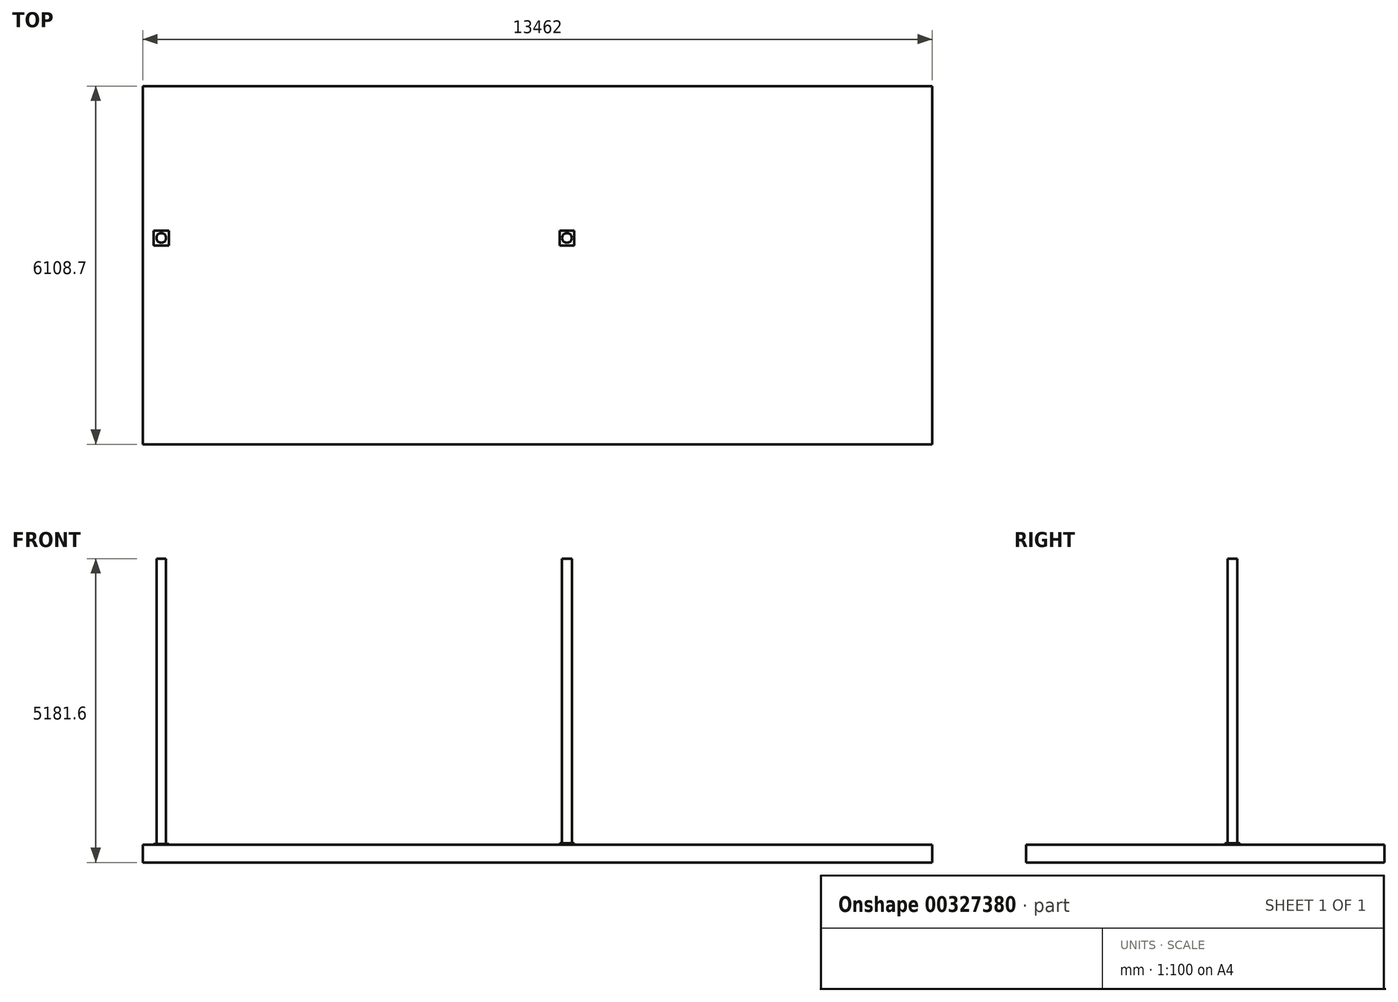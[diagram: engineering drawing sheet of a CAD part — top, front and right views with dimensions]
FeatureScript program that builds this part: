
annotation { "Feature Type Name" : "Feature", "Feature Type Description" : "" }
export const myFeature = defineFeature(function(context is Context, id is Id, definition is map)
    precondition{}
    {
        {
            var Q0;
            Q0=qCreatedBy(makeId("Top.planeOp"),FACE);
            var sketch = newSketch(context, id + "F0", { "sketchPlane" : qUnion([Q0])});
            skLineSegment(sketch, "E0.bottom", {"start": v(0, 0) * mm, "end": v(13462, 0) * mm});
            skLineSegment(sketch, "E0.top", {"start": v(0, 6108.7) * mm, "end": v(13462, 6108.7) * mm});
            skLineSegment(sketch, "E0.left", {"start": v(0, 0) * mm, "end": v(0, 6108.7) * mm});
            skLineSegment(sketch, "E0.right", {"start": v(13462, 0) * mm, "end": v(13462, 6108.7) * mm});
            skSolve(sketch);
        }
        {
            var Q0;
            Q0=makeQuery(id+"F0.imprint","IMPRINT",FACE,{"disambiguationData":[TD([[makeQuery(id+"F0.imprint","IMPRINT",EDGE,{"derivedFrom":sQuery(id+"F0.wireOp",EDGE,"E0.bottom")}),1.0]])]});
            extrude(context, id + "F1", {"entities" : qUnion([Q0]), "oppositeDirection" : true, "depth" : 304.8 * mm});
        }
        {
            var Q0;
            Q0=makeQuery(id+"F1.opExtrude","CAP_FACE",FACE,{"disambiguationData":[OSD([sQuery(id+"F0.wireOp",EDGE,"E0.bottom"),sQuery(id+"F0.wireOp",EDGE,"E0.top"),sQuery(id+"F0.wireOp",EDGE,"E0.left"),sQuery(id+"F0.wireOp",EDGE,"E0.right")])],"isStart":true});
            var sketch = newSketch(context, id + "F2", { "sketchPlane" : qUnion([Q0])});
            skLineSegment(sketch, "E1.bottom", {"start": v(190.5, 3644.9) * mm, "end": v(444.5, 3644.9) * mm});
            skLineSegment(sketch, "E1.top", {"start": v(190.5, 3390.9) * mm, "end": v(444.5, 3390.9) * mm});
            skLineSegment(sketch, "E1.left", {"start": v(190.5, 3644.9) * mm, "end": v(190.5, 3390.9) * mm});
            skLineSegment(sketch, "E1.right", {"start": v(444.5, 3644.9) * mm, "end": v(444.5, 3390.9) * mm});
            skCircle(sketch, "E2", {"center": v(317.5, 3517.9) * mm, "radius": 82.55 * mm});
            skPoint(sketch, "E2.centerSnap0", {"position": v(317.5, 3644.9) * mm});
            skPoint(sketch, "E2.centerSnap1", {"position": v(190.5, 3517.9) * mm});
            skLineSegment(sketch, "E3.bottom", {"start": v(7105.65, 3644.9) * mm, "end": v(7359.65, 3644.9) * mm});
            skLineSegment(sketch, "E3.top", {"start": v(7105.65, 3390.9) * mm, "end": v(7359.65, 3390.9) * mm});
            skLineSegment(sketch, "E3.left", {"start": v(7105.65, 3644.9) * mm, "end": v(7105.65, 3390.9) * mm});
            skLineSegment(sketch, "E3.right", {"start": v(7359.65, 3644.9) * mm, "end": v(7359.65, 3390.9) * mm});
            skCircle(sketch, "E4", {"center": v(7232.65, 3517.9) * mm, "radius": 82.55 * mm});
            skPoint(sketch, "E4.centerSnap0", {"position": v(7232.65, 3644.9) * mm});
            skPoint(sketch, "E4.centerSnap1", {"position": v(7105.65, 3517.9) * mm});
            skSolve(sketch);
        }
        {
            var Q0;
            Q0=makeQuery(id+"F2.imprint","IMPRINT",FACE,{"disambiguationData":[TD([[makeQuery(id+"F2.imprint","IMPRINT",EDGE,{"derivedFrom":sQuery(id+"F2.wireOp",EDGE,"E1.bottom")}),-1.0]])]});
            var Q1;
            Q1=sQuery(id+"F2.wireOp",EDGE,"E1.left");
            var Q2;
            Q2=sQuery(id+"F2.wireOp",EDGE,"E1.bottom");
            var Q3;
            Q3=sQuery(id+"F2.wireOp",EDGE,"E1.right");
            var Q4;
            Q4=sQuery(id+"F2.wireOp",EDGE,"E1.top");
            extrude(context, id + "F3", {"entities" : qUnion([Q0]), "operationType" : NewBodyOperationType.ADD, "surfaceEntities" : qUnion([Q1, Q2, Q3, Q4]), "depth" : 12.7 * mm, "offsetDistance" : 25.4 * mm});
        }
        {
            var Q0;
            Q0=makeQuery(id+"F2.imprint","IMPRINT",FACE,{"disambiguationData":[TD([[makeQuery(id+"F2.imprint","IMPRINT",EDGE,{"derivedFrom":sQuery(id+"F2.wireOp",EDGE,"E3.bottom")}),-1.0]])]});
            extrude(context, id + "F4", {"entities" : qUnion([Q0]), "operationType" : NewBodyOperationType.ADD, "depth" : 25.4 * mm, "offsetDistance" : 25.4 * mm});
        }
        {
            var Q0;
            Q0=makeQuery(id+"F2.imprint","IMPRINT",FACE,{"disambiguationData":[TD([[makeQuery(id+"F2.imprint","IMPRINT",EDGE,{"derivedFrom":sQuery(id+"F2.wireOp",EDGE,"E2")}),1.0]])]});
            extrude(context, id + "F5", {"entities" : qUnion([Q0]), "operationType" : NewBodyOperationType.ADD, "depth" : 4876.8 * mm, "offsetDistance" : 25.4 * mm});
        }
        {
            var Q0;
            Q0=makeQuery(id+"F2.imprint","IMPRINT",FACE,{"disambiguationData":[TD([[makeQuery(id+"F2.imprint","IMPRINT",EDGE,{"derivedFrom":sQuery(id+"F2.wireOp",EDGE,"E4")}),1.0]])]});
            extrude(context, id + "F6", {"entities" : qUnion([Q0]), "operationType" : NewBodyOperationType.ADD, "depth" : 4876.8 * mm, "offsetDistance" : 25.4 * mm});
        }
    });
